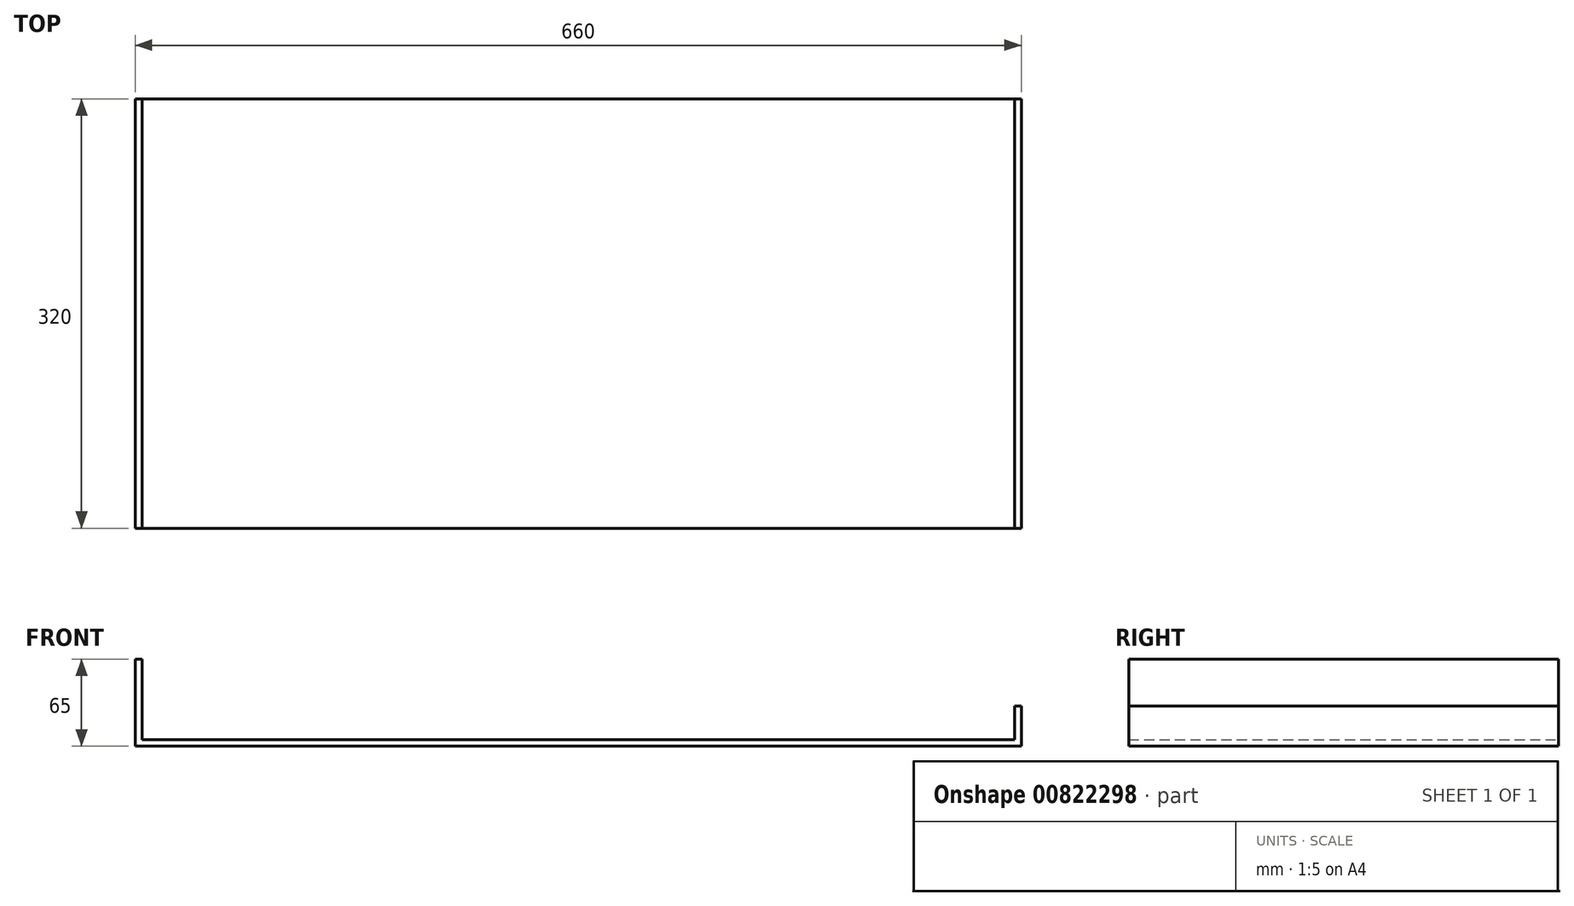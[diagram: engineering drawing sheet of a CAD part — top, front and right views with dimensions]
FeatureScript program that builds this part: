
annotation { "Feature Type Name" : "Feature", "Feature Type Description" : "" }
export const myFeature = defineFeature(function(context is Context, id is Id, definition is map)
    precondition{}
    {
        {
            var Q0;
            Q0=qCreatedBy(makeId("Front.planeOp"),FACE);
            var sketch = newSketch(context, id + "F0", { "sketchPlane" : qUnion([Q0])});
            skLineSegment(sketch, "E0.bottom", {"start": v(325, -2.5) * mm, "end": v(-325, -2.5) * mm});
            skLineSegment(sketch, "E0.top", {"start": v(325, 2.5) * mm, "end": v(-325, 2.5) * mm});
            skLineSegment(sketch, "E0.left", {"start": v(325, -2.5) * mm, "end": v(325, 2.5) * mm});
            skLineSegment(sketch, "E0.right", {"start": v(-325, -2.5) * mm, "end": v(-325, 2.5) * mm});
            skPoint(sketch, "E0.middle", {"position": v(0, 0) * mm});
            skLineSegment(sketch, "E1", {"start": v(-325, 2.5) * mm, "end": v(-325, 62.5) * mm});
            skLineSegment(sketch, "E2", {"start": v(-325, 62.5) * mm, "end": v(-330, 62.5) * mm});
            skLineSegment(sketch, "E3", {"start": v(-330, 62.5) * mm, "end": v(-330, -2.5) * mm});
            skLineSegment(sketch, "E4", {"start": v(-330, -2.5) * mm, "end": v(-325, -2.5) * mm});
            skLineSegment(sketch, "E5", {"start": v(325, 2.5) * mm, "end": v(325, 27.5) * mm});
            skLineSegment(sketch, "E6", {"start": v(325, 27.5) * mm, "end": v(330, 27.5) * mm});
            skLineSegment(sketch, "E7", {"start": v(330, 27.5) * mm, "end": v(330, -2.5) * mm});
            skLineSegment(sketch, "E8", {"start": v(330, -2.5) * mm, "end": v(325, -2.5) * mm});
            skSolve(sketch);
        }
        {
            var Q0;
            Q0 = qSketchRegion(id + "F0", true);
            extrude(context, id + "F1", {"entities" : qUnion([Q0]), "depth" : 320 * mm, "offsetDistance" : 25 * mm});
        }
    });
